# Revit family: COTTO-วาล์วเปิด-ปิดน้ำแบบก้านโยก-CT1216A
name_source: partatom
category: Plumbing Fixtures
revit_build: Autodesk Revit 2017 (Build: 20160720_1515(x64)
units: mm (PartAtom-declared; Revit-internal decimal feet)

## family parameters
Always vertical = Yes
Cut with Voids When Loaded = No
Part Type = Normal
Room Calculation Point = No
Round Connector Dimension = Use Diameter
Shared = No
Work Plane-Based = No

## types (1)
- COTTO-วาล์วเปิด-ปิดน้ำแบบก้านโยก-CT1216A
    Barcode = 8852410121354
    CW Connection = No
    Code = CT1216A
    Color = โครเมี่ยม
    Description = วาล์วเปิด-ปิดน้ำแบบก้านโยก
    Drain = 0 mm  [stored 0 ft]
    Manufacturer = COTTO
    Material = SCG โลหะ
    Sap Code = Z231CT1216AXXXXX11
    URL = https://www.cotto.com
    Waste Connection = No
    Water Supply = 0 mm  [stored 0 ft]
    กว้าง (มม.) = 12 mm  [stored 0.0393701 ft]
    น้ำหนัก (kg.) = 0.85
    ยาว (มม.) = 12 mm  [stored 0.0393701 ft]
    รูปแบบการติดตั้ง = ติดบนผนัง
    สูง (มม.) = 0 mm  [stored 0 ft]
    แรงดันน้ำ = 1.5 บาร์

note: [stored X ft] marks values corroborated as IEEE doubles in the binary element streams (Revit-internal decimal feet)

## geometry (parser evidence)
native form markers: Sweep x3
no freeform markers — native parametric forms only
